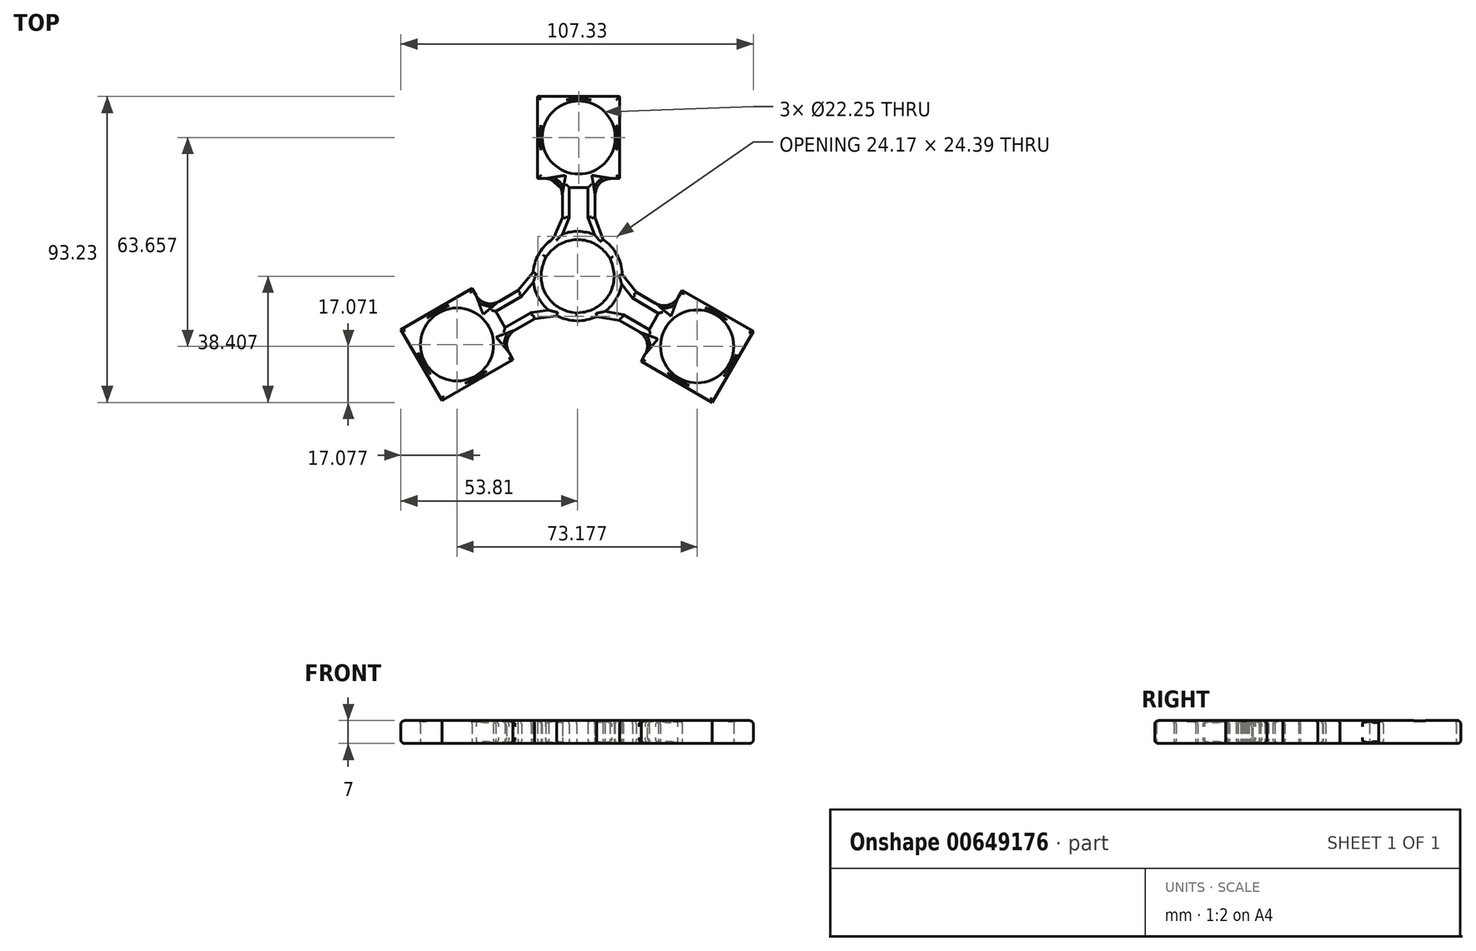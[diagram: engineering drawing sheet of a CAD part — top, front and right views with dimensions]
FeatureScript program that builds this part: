
annotation { "Feature Type Name" : "Feature", "Feature Type Description" : "" }
export const myFeature = defineFeature(function(context is Context, id is Id, definition is map)
    precondition{}
    {
        {
            var Q0;
            Q0=qCreatedBy(makeId("Top.planeOp"),FACE);
            var sketch = newSketch(context, id + "F0", { "sketchPlane" : qUnion([Q0])});
            skCircle(sketch, "E0", {"center": v(0, 0) * mm, "radius": 11.13 * mm});
            skCircle(sketch, "E1.0.1.0", {"center": v(0.33, 42.25) * mm, "radius": 11.13 * mm});
            skLineSegment(sketch, "E2.bottom", {"start": v(12.83, 54.75) * mm, "end": v(-12.17, 54.75) * mm});
            skLineSegment(sketch, "E2.top", {"start": v(12.83, 29.75) * mm, "end": v(-12.17, 29.75) * mm});
            skLineSegment(sketch, "E2.left", {"start": v(12.83, 54.75) * mm, "end": v(12.83, 29.75) * mm});
            skLineSegment(sketch, "E2.right", {"start": v(-12.17, 54.75) * mm, "end": v(-12.17, 29.75) * mm});
            skLineSegment(sketch, "E3", {"start": v(-4.67, 29.75) * mm, "end": v(-4.67, 17.87) * mm});
            skLineSegment(sketch, "E4", {"start": v(-4.67, 17.87) * mm, "end": v(-10.29, 4.24) * mm});
            skLineSegment(sketch, "E5", {"start": v(5.33, 29.75) * mm, "end": v(5.33, 17.9) * mm});
            skLineSegment(sketch, "E6", {"start": v(5.33, 17.9) * mm, "end": v(10.45, 3.8) * mm});
            skLineSegment(sketch, "E7", {"start": v(-2.54, 27) * mm, "end": v(-2.54, 17.8) * mm});
            skLineSegment(sketch, "E8", {"start": v(-2.54, 17.8) * mm, "end": v(-4.82, 12.26) * mm});
            skLineSegment(sketch, "E9", {"start": v(5.25, 12.26) * mm, "end": v(3.2, 17.9) * mm});
            skLineSegment(sketch, "E10", {"start": v(3.2, 17.9) * mm, "end": v(3.2, 27) * mm});
            skLineSegment(sketch, "E11", {"start": v(3.2, 27) * mm, "end": v(-2.54, 27) * mm});
            skCircle(sketch, "E12", {"center": v(0, 0) * mm, "radius": 13.63 * mm});
            skCircle(sketch, "E13.1.0", {"center": v(-36.75, -20.84) * mm, "radius": 11.13 * mm});
            skLineSegment(sketch, "E13.1.1", {"start": v(-28.43, -10.26) * mm, "end": v(-18.16, -4.33) * mm});
            skLineSegment(sketch, "E13.1.2", {"start": v(-32.18, -3.76) * mm, "end": v(-19.68, -25.42) * mm});
            skLineSegment(sketch, "E13.1.3", {"start": v(-53.83, -16.26) * mm, "end": v(-32.18, -3.76) * mm});
            skLineSegment(sketch, "E13.1.4", {"start": v(-41.33, -37.92) * mm, "end": v(-19.68, -25.42) * mm});
            skLineSegment(sketch, "E13.1.5", {"start": v(-53.83, -16.26) * mm, "end": v(-41.33, -37.92) * mm});
            skLineSegment(sketch, "E13.1.6", {"start": v(-22.11, -15.7) * mm, "end": v(-14.15, -11.1) * mm});
            skLineSegment(sketch, "E13.1.7", {"start": v(-17.1, -6.18) * mm, "end": v(-24.98, -10.73) * mm});
            skLineSegment(sketch, "E13.1.8", {"start": v(-24.98, -10.73) * mm, "end": v(-22.11, -15.7) * mm});
            skLineSegment(sketch, "E13.1.9", {"start": v(-13.24, -1.58) * mm, "end": v(-17.1, -6.18) * mm});
            skLineSegment(sketch, "E13.1.10", {"start": v(-14.15, -11.1) * mm, "end": v(-8.2, -10.3) * mm});
            skLineSegment(sketch, "E13.1.12", {"start": v(-13.14, -12.98) * mm, "end": v(1.47, -11.03) * mm});
            skLineSegment(sketch, "E13.1.13", {"start": v(-18.16, -4.33) * mm, "end": v(-8.52, 7.15) * mm});
            skLineSegment(sketch, "E13.1.14", {"start": v(-23.43, -18.92) * mm, "end": v(-13.14, -12.98) * mm});
            skCircle(sketch, "E13.2.0", {"center": v(36.42, -21.4) * mm, "radius": 11.13 * mm});
            skLineSegment(sketch, "E13.2.1", {"start": v(23.1, -19.49) * mm, "end": v(12.84, -13.56) * mm});
            skLineSegment(sketch, "E13.2.2", {"start": v(19.35, -25.98) * mm, "end": v(31.85, -4.33) * mm});
            skLineSegment(sketch, "E13.2.3", {"start": v(41, -38.48) * mm, "end": v(19.35, -25.98) * mm});
            skLineSegment(sketch, "E13.2.4", {"start": v(53.5, -16.83) * mm, "end": v(31.85, -4.33) * mm});
            skLineSegment(sketch, "E13.2.5", {"start": v(41, -38.48) * mm, "end": v(53.5, -16.83) * mm});
            skLineSegment(sketch, "E13.2.6", {"start": v(24.65, -11.3) * mm, "end": v(16.69, -6.7) * mm});
            skLineSegment(sketch, "E13.2.7", {"start": v(13.9, -11.72) * mm, "end": v(21.78, -16.27) * mm});
            skLineSegment(sketch, "E13.2.8", {"start": v(21.78, -16.27) * mm, "end": v(24.65, -11.3) * mm});
            skLineSegment(sketch, "E13.2.9", {"start": v(8, -10.68) * mm, "end": v(13.9, -11.72) * mm});
            skLineSegment(sketch, "E13.2.10", {"start": v(16.69, -6.7) * mm, "end": v(13.03, -1.96) * mm});
            skLineSegment(sketch, "E13.2.12", {"start": v(17.81, -4.9) * mm, "end": v(8.81, 6.8) * mm});
            skLineSegment(sketch, "E13.2.13", {"start": v(12.84, -13.56) * mm, "end": v(-1.93, -10.96) * mm});
            skLineSegment(sketch, "E13.2.14", {"start": v(28.1, -10.83) * mm, "end": v(17.81, -4.9) * mm});
            skSolve(sketch);
        }
        {
            var Q0;
            Q0=qSketchRegion(id+"F0",true);
            extrude(context, id + "F1", {"entities" : qUnion([Q0]), "depth" : 7 * mm, "offsetDistance" : 25 * mm});
        }
        {
            var Q0;
            Q0=makeQuery(id+"F1.opExtrude","SWEPT_EDGE",EDGE,{"disambiguationData":[OSD([sQuery(id+"F0.wireOp",EDGE,"E4"),sQuery(id+"F0.wireOp",EDGE,"E12")])]});
            fillet(context, id + "F2", {"entities" : qUnion([Q0]), "radius" : 5 * mm, "tangentPropagation" : true, "allowEdgeOverflow" : false});
        }
        {
            var Q0;
            Q0=makeQuery(id+"F1.opExtrude","CAP_FACE",FACE,{"disambiguationData":[OSD([sQuery(id+"F0.wireOp",EDGE,"E0"),sQuery(id+"F0.wireOp",EDGE,"E1.0.1.0"),sQuery(id+"F0.wireOp",EDGE,"E2.bottom"),sQuery(id+"F0.wireOp",EDGE,"E2.top"),sQuery(id+"F0.wireOp",EDGE,"E2.left"),sQuery(id+"F0.wireOp",EDGE,"E2.right"),sQuery(id+"F0.wireOp",EDGE,"E3"),sQuery(id+"F0.wireOp",EDGE,"E4"),sQuery(id+"F0.wireOp",EDGE,"E5"),sQuery(id+"F0.wireOp",EDGE,"E6"),sQuery(id+"F0.wireOp",EDGE,"E7"),sQuery(id+"F0.wireOp",EDGE,"E8"),sQuery(id+"F0.wireOp",EDGE,"E9"),sQuery(id+"F0.wireOp",EDGE,"E10"),sQuery(id+"F0.wireOp",EDGE,"E11"),sQuery(id+"F0.wireOp",EDGE,"E12"),sQuery(id+"F0.wireOp",EDGE,"E13.1.0"),sQuery(id+"F0.wireOp",EDGE,"E13.1.1"),sQuery(id+"F0.wireOp",EDGE,"E13.1.2"),sQuery(id+"F0.wireOp",EDGE,"E13.1.3"),sQuery(id+"F0.wireOp",EDGE,"E13.1.4"),sQuery(id+"F0.wireOp",EDGE,"E13.1.5"),sQuery(id+"F0.wireOp",EDGE,"E13.1.6"),sQuery(id+"F0.wireOp",EDGE,"E13.1.7"),sQuery(id+"F0.wireOp",EDGE,"E13.1.8"),sQuery(id+"F0.wireOp",EDGE,"E13.1.9"),sQuery(id+"F0.wireOp",EDGE,"E13.1.10"),sQuery(id+"F0.wireOp",EDGE,"E13.1.12"),sQuery(id+"F0.wireOp",EDGE,"E13.1.13"),sQuery(id+"F0.wireOp",EDGE,"E13.1.14"),sQuery(id+"F0.wireOp",EDGE,"E13.2.0"),sQuery(id+"F0.wireOp",EDGE,"E13.2.1"),sQuery(id+"F0.wireOp",EDGE,"E13.2.2"),sQuery(id+"F0.wireOp",EDGE,"E13.2.3"),sQuery(id+"F0.wireOp",EDGE,"E13.2.4"),sQuery(id+"F0.wireOp",EDGE,"E13.2.5"),sQuery(id+"F0.wireOp",EDGE,"E13.2.6"),sQuery(id+"F0.wireOp",EDGE,"E13.2.7"),sQuery(id+"F0.wireOp",EDGE,"E13.2.8"),sQuery(id+"F0.wireOp",EDGE,"E13.2.9"),sQuery(id+"F0.wireOp",EDGE,"E13.2.10"),sQuery(id+"F0.wireOp",EDGE,"E13.2.12"),sQuery(id+"F0.wireOp",EDGE,"E13.2.13"),sQuery(id+"F0.wireOp",EDGE,"E13.2.14")])],"isStart":false});
            fillet(context, id + "F3", {"entities" : qUnion([Q0]), "radius" : 1 * mm, "tangentPropagation" : true, "allowEdgeOverflow" : false});
        }
        {
            var Q0;
            Q0=makeQuery(id+"F1.opExtrude","CAP_FACE",FACE,{"disambiguationData":[OSD([sQuery(id+"F0.wireOp",EDGE,"E0"),sQuery(id+"F0.wireOp",EDGE,"E1.0.1.0"),sQuery(id+"F0.wireOp",EDGE,"E2.bottom"),sQuery(id+"F0.wireOp",EDGE,"E2.top"),sQuery(id+"F0.wireOp",EDGE,"E2.left"),sQuery(id+"F0.wireOp",EDGE,"E2.right"),sQuery(id+"F0.wireOp",EDGE,"E3"),sQuery(id+"F0.wireOp",EDGE,"E4"),sQuery(id+"F0.wireOp",EDGE,"E5"),sQuery(id+"F0.wireOp",EDGE,"E6"),sQuery(id+"F0.wireOp",EDGE,"E7"),sQuery(id+"F0.wireOp",EDGE,"E8"),sQuery(id+"F0.wireOp",EDGE,"E9"),sQuery(id+"F0.wireOp",EDGE,"E10"),sQuery(id+"F0.wireOp",EDGE,"E11"),sQuery(id+"F0.wireOp",EDGE,"E12"),sQuery(id+"F0.wireOp",EDGE,"E13.1.0"),sQuery(id+"F0.wireOp",EDGE,"E13.1.1"),sQuery(id+"F0.wireOp",EDGE,"E13.1.2"),sQuery(id+"F0.wireOp",EDGE,"E13.1.3"),sQuery(id+"F0.wireOp",EDGE,"E13.1.4"),sQuery(id+"F0.wireOp",EDGE,"E13.1.5"),sQuery(id+"F0.wireOp",EDGE,"E13.1.6"),sQuery(id+"F0.wireOp",EDGE,"E13.1.7"),sQuery(id+"F0.wireOp",EDGE,"E13.1.8"),sQuery(id+"F0.wireOp",EDGE,"E13.1.9"),sQuery(id+"F0.wireOp",EDGE,"E13.1.10"),sQuery(id+"F0.wireOp",EDGE,"E13.1.12"),sQuery(id+"F0.wireOp",EDGE,"E13.1.13"),sQuery(id+"F0.wireOp",EDGE,"E13.1.14"),sQuery(id+"F0.wireOp",EDGE,"E13.2.0"),sQuery(id+"F0.wireOp",EDGE,"E13.2.1"),sQuery(id+"F0.wireOp",EDGE,"E13.2.2"),sQuery(id+"F0.wireOp",EDGE,"E13.2.3"),sQuery(id+"F0.wireOp",EDGE,"E13.2.4"),sQuery(id+"F0.wireOp",EDGE,"E13.2.5"),sQuery(id+"F0.wireOp",EDGE,"E13.2.6"),sQuery(id+"F0.wireOp",EDGE,"E13.2.7"),sQuery(id+"F0.wireOp",EDGE,"E13.2.8"),sQuery(id+"F0.wireOp",EDGE,"E13.2.9"),sQuery(id+"F0.wireOp",EDGE,"E13.2.10"),sQuery(id+"F0.wireOp",EDGE,"E13.2.12"),sQuery(id+"F0.wireOp",EDGE,"E13.2.13"),sQuery(id+"F0.wireOp",EDGE,"E13.2.14")])],"isStart":true});
            fillet(context, id + "F4", {"entities" : qUnion([Q0]), "radius" : 1 * mm, "tangentPropagation" : true, "allowEdgeOverflow" : false});
        }
        {
            var Q0;
            Q0=makeQuery(id+"F1.opExtrude","SWEPT_EDGE",EDGE,{"disambiguationData":[OSD([sQuery(id+"F0.wireOp",EDGE,"E13.1.2"),sQuery(id+"F0.wireOp",EDGE,"E13.1.14")])]});
            var Q1;
            Q1=makeQuery(id+"F1.opExtrude","SWEPT_EDGE",EDGE,{"disambiguationData":[OSD([sQuery(id+"F0.wireOp",EDGE,"E13.1.1"),sQuery(id+"F0.wireOp",EDGE,"E13.1.2")])]});
            var Q2;
            Q2=makeQuery(id+"F1.opExtrude","SWEPT_EDGE",EDGE,{"disambiguationData":[OSD([sQuery(id+"F0.wireOp",EDGE,"E2.top"),sQuery(id+"F0.wireOp",EDGE,"E5")])]});
            var Q3;
            Q3=makeQuery(id+"F1.opExtrude","SWEPT_EDGE",EDGE,{"disambiguationData":[OSD([sQuery(id+"F0.wireOp",EDGE,"E2.top"),sQuery(id+"F0.wireOp",EDGE,"E3")])]});
            var Q4;
            Q4=makeQuery(id+"F1.opExtrude","SWEPT_EDGE",EDGE,{"disambiguationData":[OSD([sQuery(id+"F0.wireOp",EDGE,"E13.2.1"),sQuery(id+"F0.wireOp",EDGE,"E13.2.2")])]});
            var Q5;
            Q5=makeQuery(id+"F1.opExtrude","SWEPT_EDGE",EDGE,{"disambiguationData":[OSD([sQuery(id+"F0.wireOp",EDGE,"E13.2.2"),sQuery(id+"F0.wireOp",EDGE,"E13.2.14")])]});
            fillet(context, id + "F5", {"entities" : qUnion([Q0, Q1, Q2, Q3, Q4, Q5]), "radius" : 5 * mm, "tangentPropagation" : true, "allowEdgeOverflow" : false});
        }
    });
